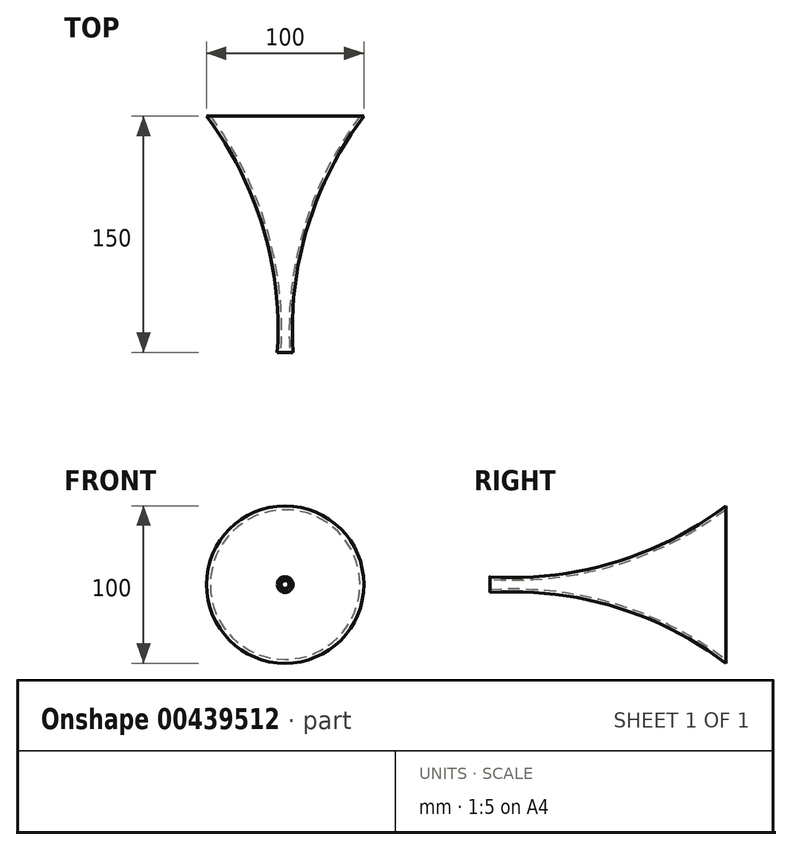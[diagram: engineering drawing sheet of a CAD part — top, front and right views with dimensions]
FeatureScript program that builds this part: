
annotation { "Feature Type Name" : "Feature", "Feature Type Description" : "" }
export const myFeature = defineFeature(function(context is Context, id is Id, definition is map)
    precondition{}
    {
        {
            var Q0;
            Q0=qCreatedBy(makeId("Right.planeOp"),FACE);
            var sketch = newSketch(context, id + "F0", { "sketchPlane" : qUnion([Q0])});
            skLineSegment(sketch, "E0", {"start": v(-50.62, 0) * mm, "end": v(44.29, 0) * mm, "construction": true});
            skArc(sketch, "E1", {"start": v(-14.39, 3) * mm, "mid": v(64.57, 11.92) * mm, "end": v(135.61, 47.5) * mm});
            skArc(sketch, "E2", {"start": v(-14.39, 5) * mm, "mid": v(64.65, 14.03) * mm, "end": v(135.61, 50) * mm});
            skLineSegment(sketch, "E3", {"start": v(-14.39, 5) * mm, "end": v(-14.39, 3) * mm});
            skLineSegment(sketch, "E4", {"start": v(135.61, 47.5) * mm, "end": v(135.61, 50) * mm});
            skSolve(sketch);
        }
        {
            var Q0;
            Q0=makeQuery(id+"F0.imprint","IMPRINT",FACE,{"disambiguationData":[TD([[makeQuery(id+"F0.imprint","IMPRINT",EDGE,{"derivedFrom":sQuery(id+"F0.wireOp",EDGE,"E1")}),1.0]])]});
            var Q1;
            Q1=sQuery(id+"F0.wireOp",EDGE,"E0");
            revolve(context, id + "F1", {"entities" : qUnion([Q0]), "axis" : qUnion([Q1]), "revolveType" : RevolveType.FULL});
        }
    });
